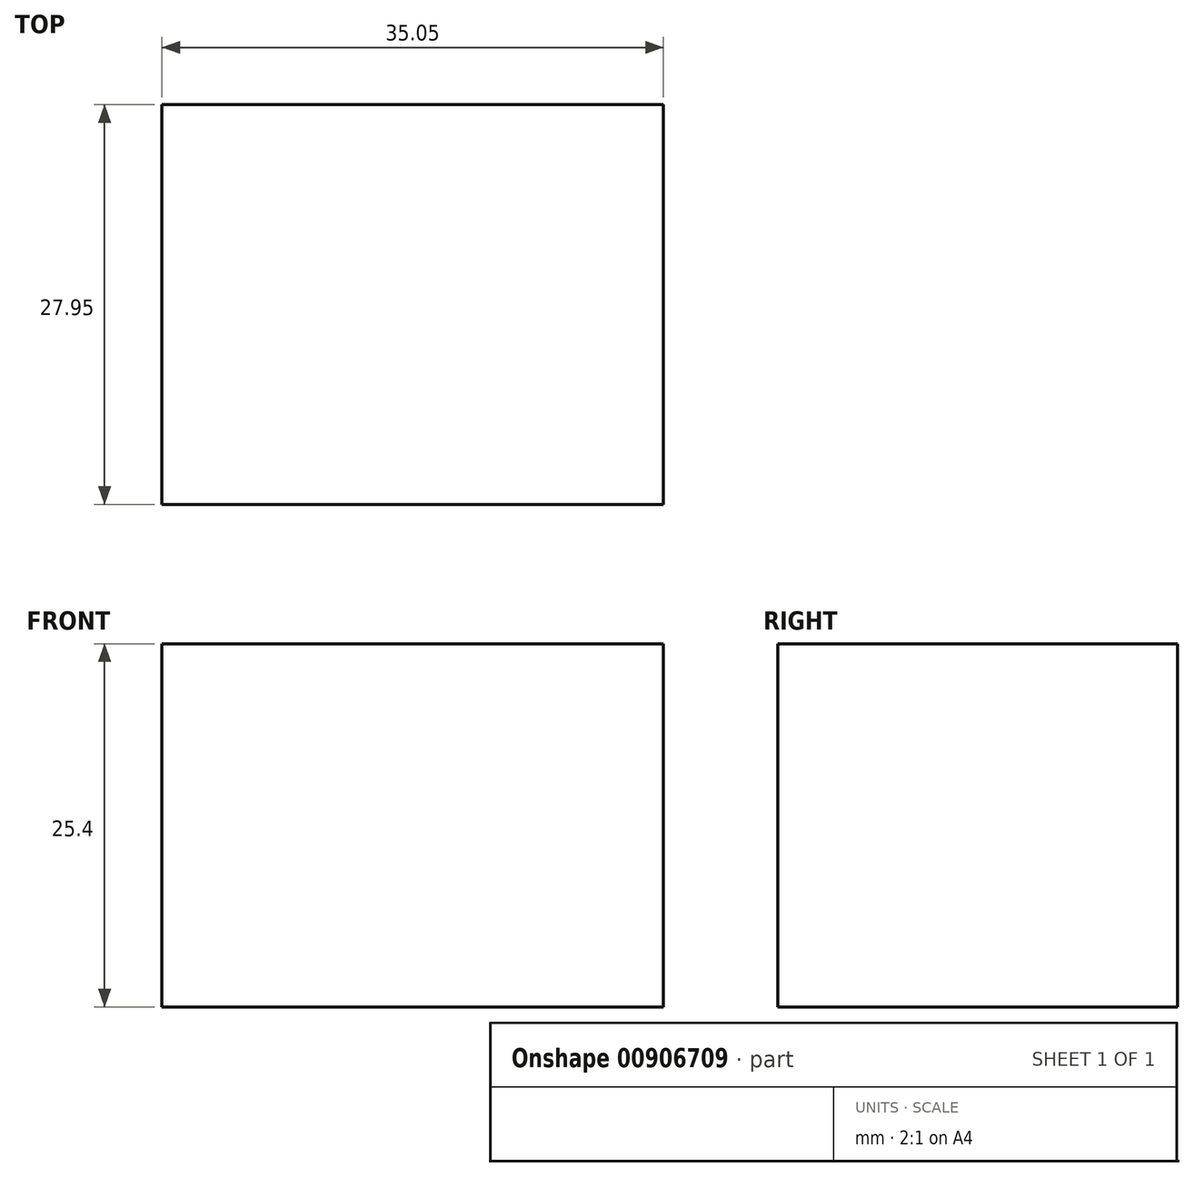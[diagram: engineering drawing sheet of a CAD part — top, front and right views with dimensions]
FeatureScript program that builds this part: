
annotation { "Feature Type Name" : "Feature", "Feature Type Description" : "" }
export const myFeature = defineFeature(function(context is Context, id is Id, definition is map)
    precondition{}
    {
        {
            var Q0;
            Q0=qCreatedBy(makeId("Top.planeOp"),FACE);
            var sketch = newSketch(context, id + "F0", { "sketchPlane" : qUnion([Q0])});
            skLineSegment(sketch, "E0.bottom", {"start": v(0, 0) * mm, "end": v(35.05, 0) * mm});
            skLineSegment(sketch, "E0.top", {"start": v(0, -27.95) * mm, "end": v(35.05, -27.95) * mm});
            skLineSegment(sketch, "E0.left", {"start": v(0, 0) * mm, "end": v(0, -27.95) * mm});
            skLineSegment(sketch, "E0.right", {"start": v(35.05, 0) * mm, "end": v(35.05, -27.95) * mm});
            skSolve(sketch);
        }
        {
            var Q0;
            Q0=makeQuery(id+"F0.imprint","IMPRINT",FACE,{"disambiguationData":[TD([[makeQuery(id+"F0.imprint","IMPRINT",EDGE,{"derivedFrom":sQuery(id+"F0.wireOp",EDGE,"E0.bottom")}),-1.0]])]});
            extrude(context, id + "F1", {"entities" : qUnion([Q0]), "depth" : 25.4 * mm, "offsetDistance" : 25.4 * mm});
        }
    });
